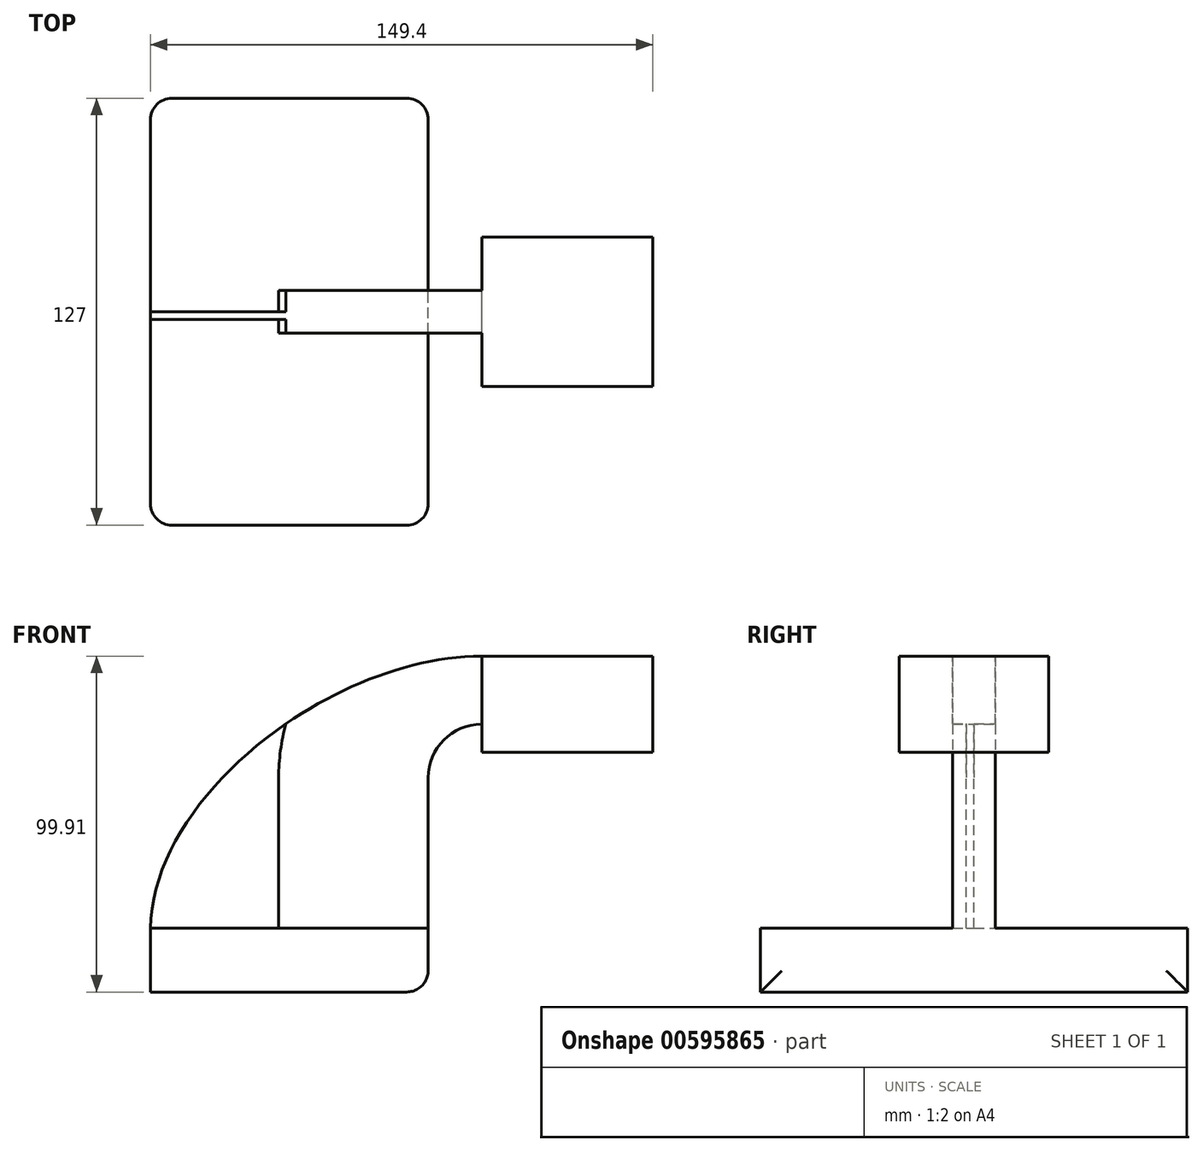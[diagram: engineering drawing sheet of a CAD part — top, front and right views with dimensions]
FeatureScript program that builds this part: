
annotation { "Feature Type Name" : "Feature", "Feature Type Description" : "" }
export const myFeature = defineFeature(function(context is Context, id is Id, definition is map)
    precondition{}
    {
        {
            var Q0;
            Q0=qCreatedBy(makeId("Front.planeOp"),FACE);
            var sketch = newSketch(context, id + "F0", { "sketchPlane" : qUnion([Q0])});
            skLineSegment(sketch, "E0.bottom", {"start": v(41.27, 9.53) * mm, "end": v(-41.28, 9.53) * mm});
            skLineSegment(sketch, "E0.top", {"start": v(41.28, -9.52) * mm, "end": v(-41.27, -9.52) * mm});
            skLineSegment(sketch, "E0.left", {"start": v(41.28, 9.53) * mm, "end": v(41.28, -9.52) * mm});
            skLineSegment(sketch, "E0.right", {"start": v(-41.28, 9.53) * mm, "end": v(-41.28, -9.52) * mm});
            skPoint(sketch, "E0.middle", {"position": v(0, 0) * mm});
            skLineSegment(sketch, "E1.bottom", {"start": v(108.12, 90.38) * mm, "end": v(57.32, 90.38) * mm});
            skLineSegment(sketch, "E1.top", {"start": v(108.12, 61.8) * mm, "end": v(57.32, 61.8) * mm});
            skLineSegment(sketch, "E1.left", {"start": v(108.12, 90.38) * mm, "end": v(108.12, 61.8) * mm});
            skLineSegment(sketch, "E1.right", {"start": v(57.32, 90.38) * mm, "end": v(57.32, 61.8) * mm});
            skPoint(sketch, "E1.middle", {"position": v(82.72, 76.1) * mm});
            skLineSegment(sketch, "E2", {"start": v(41.27, 9.53) * mm, "end": v(41.27, 54.25) * mm});
            skArc(sketch, "E3", {"start": v(41.27, 54.25) * mm, "mid": v(45.92, 65.47) * mm, "end": v(57.15, 70.12) * mm});
            skLineSegment(sketch, "E4", {"start": v(57.15, 70.12) * mm, "end": v(74.36, 70.12) * mm});
            skLineSegment(sketch, "E5.0", {"start": v(57.15, 114.57) * mm, "end": v(74.36, 114.57) * mm});
            skArc(sketch, "E5.1", {"start": v(-3.18, 54.25) * mm, "mid": v(14.5, 96.9) * mm, "end": v(57.15, 114.57) * mm});
            skLineSegment(sketch, "E5.2", {"start": v(-3.18, 9.53) * mm, "end": v(-3.18, 54.25) * mm});
            skFitSpline(sketch, "E6", {"points": [v(-41.28, 9.52) * mm, v(57.32, 90.38) * mm], "startDerivative": vector(1.52, 118.38) * mm, "endDerivative": vector(132.98, -0.08) * mm});
            skSolve(sketch);
        }
        {
            var Q0;
            Q0=makeQuery(id+"F0.imprint","IMPRINT",FACE,{"disambiguationData":[TD([[makeQuery(id+"F0.imprint","IMPRINT",EDGE,{"derivedFrom":sQuery(id+"F0.wireOp",EDGE,"E0.top")}),-1.0]])]});
            extrude(context, id + "F1", {"entities" : qUnion([Q0]), "endBound" : BoundingType.SYMMETRIC, "depth" : 127 * mm, "offsetDistance" : 25.4 * mm});
        }
        {
            var Q0;
            {var subQ1=sQuery(id+"F0.wireOp",EDGE,"E2");Q0=makeQuery(id+"F0.imprint","IMPRINT",FACE,{"disambiguationData":[TD([[makeQuery(id+"F0.imprint","IMPRINT",EDGE,{"derivedFrom":subQ1}),1.0]])]});}
            extrude(context, id + "F2", {"entities" : qUnion([Q0]), "operationType" : NewBodyOperationType.ADD, "endBound" : BoundingType.SYMMETRIC, "depth" : 12.7 * mm, "offsetDistance" : 25.4 * mm});
        }
        {
            var Q0;
            {var subQ1=sQuery(id+"F0.wireOp",EDGE,"E1.bottom");Q0=makeQuery(id+"F0.imprint","IMPRINT",FACE,{"disambiguationData":[TD([[makeQuery(id+"F0.imprint","IMPRINT",EDGE,{"derivedFrom":subQ1}),1.0]])]});}
            extrude(context, id + "F3", {"entities" : qUnion([Q0]), "operationType" : NewBodyOperationType.ADD, "endBound" : BoundingType.SYMMETRIC, "depth" : 44.45 * mm, "offsetDistance" : 25.4 * mm});
        }
        {
            var Q0;
            {var subQ3=sQuery(id+"F0.wireOp",EDGE,"E5.2");Q0=makeQuery(id+"F0.imprint","IMPRINT",FACE,{"disambiguationData":[TD([[makeQuery(id+"F0.imprint","IMPRINT",EDGE,{"derivedFrom":subQ3}),1.0]])]});}
            extrude(context, id + "F4", {"entities" : qUnion([Q0]), "operationType" : NewBodyOperationType.ADD, "depth" : 2.3 * mm, "offsetDistance" : 25.4 * mm});
        }
        {
            var Q0;
            Q0=makeQuery(id+"F1.opExtrude","CAP_EDGE",EDGE,{"disambiguationData":[OSD([sQuery(id+"F0.wireOp",EDGE,"E0.left")])],"isStart":true});
            var Q1;
            Q1=makeQuery(id+"F1.opExtrude","CAP_EDGE",EDGE,{"disambiguationData":[OSD([sQuery(id+"F0.wireOp",EDGE,"E0.right")])],"isStart":true});
            var Q2;
            Q2=makeQuery(id+"F1.opExtrude","CAP_EDGE",EDGE,{"disambiguationData":[OSD([sQuery(id+"F0.wireOp",EDGE,"E0.left")])],"isStart":false});
            var Q3;
            Q3=makeQuery(id+"F1.opExtrude","CAP_EDGE",EDGE,{"disambiguationData":[OSD([sQuery(id+"F0.wireOp",EDGE,"E0.right")])],"isStart":false});
            var Q4;
            Q4=makeQuery(id+"F1.opExtrude","SWEPT_EDGE",EDGE,{"disambiguationData":[OSD([sQuery(id+"F0.wireOp",EDGE,"E0.top"),sQuery(id+"F0.wireOp",EDGE,"E0.left")])]});
            fillet(context, id + "F5", {"entities" : qUnion([Q0, Q1, Q2, Q3, Q4]), "radius" : 6.35 * mm, "tangentPropagation" : true, "allowEdgeOverflow" : false});
        }
    });
